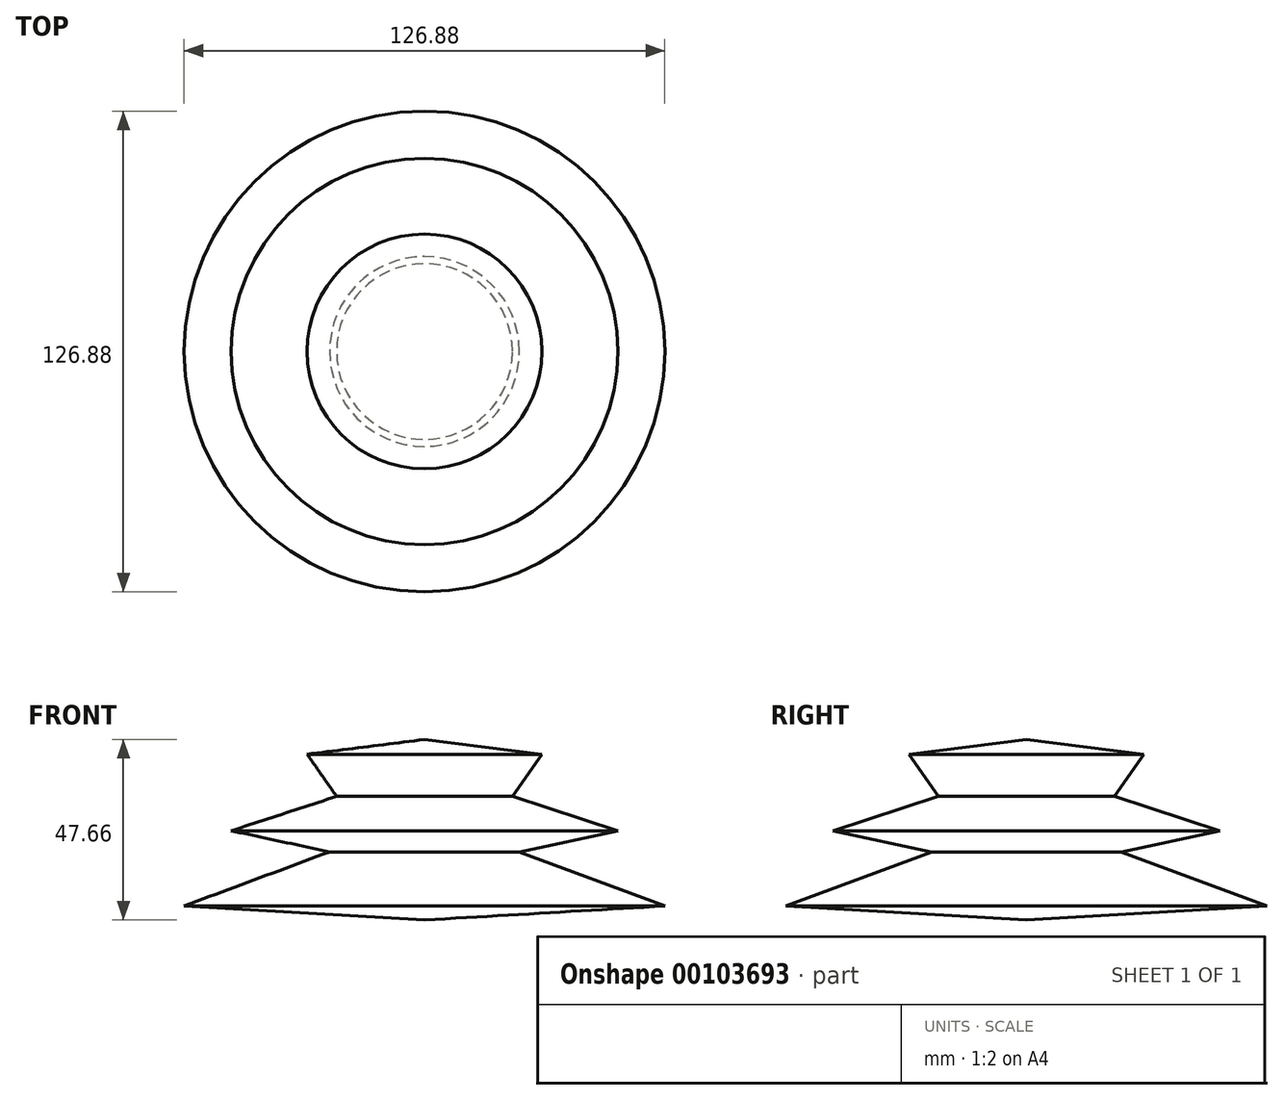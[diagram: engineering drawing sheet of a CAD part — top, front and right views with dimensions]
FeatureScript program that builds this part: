
annotation { "Feature Type Name" : "Feature", "Feature Type Description" : "" }
export const myFeature = defineFeature(function(context is Context, id is Id, definition is map)
    precondition{}
    {
        {
            var Q0;
            Q0=qCreatedBy(makeId("Front.planeOp"),FACE);
            var sketch = newSketch(context, id + "F0", { "sketchPlane" : qUnion([Q0])});
            skLineSegment(sketch, "E0", {"start": v(0, 0) * mm, "end": v(0, 47.66) * mm});
            skLineSegment(sketch, "E1", {"start": v(0, 47.66) * mm, "end": v(31, 43.77) * mm});
            skLineSegment(sketch, "E2", {"start": v(31, 43.77) * mm, "end": v(23.2, 32.64) * mm});
            skLineSegment(sketch, "E3", {"start": v(23.2, 32.64) * mm, "end": v(51.02, 23.56) * mm});
            skLineSegment(sketch, "E4", {"start": v(51.02, 23.56) * mm, "end": v(25.06, 18) * mm});
            skLineSegment(sketch, "E5", {"start": v(25.06, 18) * mm, "end": v(63.44, 3.72) * mm});
            skLineSegment(sketch, "E6", {"start": v(63.44, 3.72) * mm, "end": v(0, 0) * mm});
            skSolve(sketch);
        }
        {
            var Q0;
            Q0 = qSketchRegion(id + "F0", true);
            var Q1;
            Q1=sQuery(id+"F0.wireOp",EDGE,"E0");
            revolve(context, id + "F1", {"entities" : qUnion([Q0]), "axis" : qUnion([Q1]), "revolveType" : RevolveType.FULL});
        }
    });
